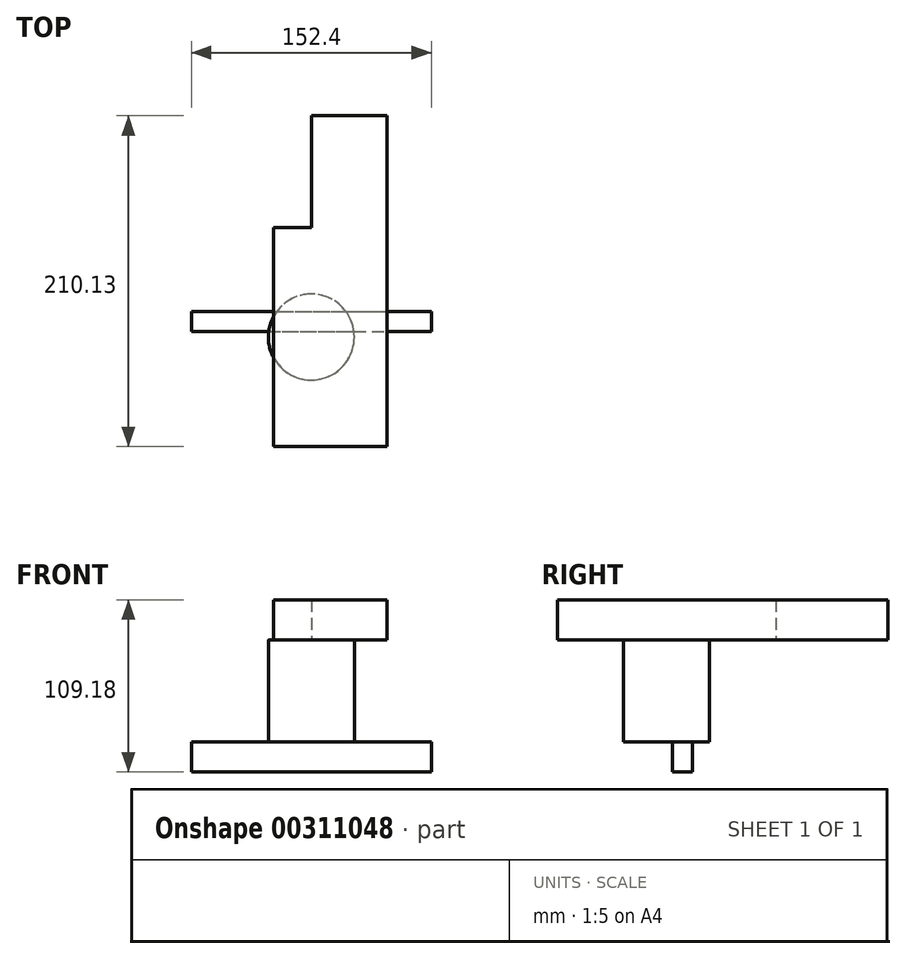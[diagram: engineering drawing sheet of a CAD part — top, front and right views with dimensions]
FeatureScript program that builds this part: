
annotation { "Feature Type Name" : "Feature", "Feature Type Description" : "" }
export const myFeature = defineFeature(function(context is Context, id is Id, definition is map)
    precondition{}
    {
        {
            var Q0;
            Q0=qCreatedBy(makeId("Front.planeOp"),FACE);
            var sketch = newSketch(context, id + "F0", { "sketchPlane" : qUnion([Q0])});
            skLineSegment(sketch, "E0.bottom", {"start": v(-76.2, -9.53) * mm, "end": v(76.2, -9.53) * mm});
            skLineSegment(sketch, "E0.top", {"start": v(-76.2, 9.53) * mm, "end": v(76.2, 9.53) * mm, "construction": true});
            skLineSegment(sketch, "E0.left", {"start": v(-76.2, 9.53) * mm, "end": v(-76.2, -9.53) * mm});
            skLineSegment(sketch, "E0.right", {"start": v(76.2, 9.53) * mm, "end": v(76.2, -9.52) * mm});
            skPoint(sketch, "E0.middle", {"position": v(0, 0) * mm});
            skLineSegment(sketch, "E1", {"start": v(-76.2, 9.53) * mm, "end": v(76.2, 9.53) * mm});
            skSolve(sketch);
        }
        {
            var Q0;
            Q0 = qSketchRegion(id + "F0", true);
            extrude(context, id + "F1", {"entities" : qUnion([Q0]), "depth" : 12.7 * mm});
        }
        {
            var Q0;
            Q0=makeQuery(id+"F1.opExtrude","SWEPT_FACE",FACE,{"disambiguationData":[OSD([sQuery(id+"F0.wireOp",EDGE,"E1")])]});
            var sketch = newSketch(context, id + "F2", { "sketchPlane" : qUnion([Q0])});
            skCircle(sketch, "E2", {"center": v(0, -16.31) * mm, "radius": 27.3 * mm});
            skSolve(sketch);
        }
        {
            var Q0;
            Q0 = qSketchRegion(id + "F2", true);
            extrude(context, id + "F3", {"entities" : qUnion([Q0]), "operationType" : NewBodyOperationType.ADD, "depth" : 64.73 * mm});
        }
        {
            var Q0;
            Q0=makeQuery(id+"F3.opExtrude","CAP_FACE",FACE,{"disambiguationData":[OSD([sQuery(id+"F2.wireOp",EDGE,"E2")])],"isStart":false});
            var sketch = newSketch(context, id + "F4", { "sketchPlane" : qUnion([Q0])});
            skLineSegment(sketch, "E3.bottom", {"start": v(0, -16.31) * mm, "end": v(0, -16.31) * mm});
            skLineSegment(sketch, "E3.top", {"start": v(0, -16.31) * mm, "end": v(0, -16.31) * mm});
            skLineSegment(sketch, "E3.left", {"start": v(0, -16.31) * mm, "end": v(0, -16.31) * mm});
            skLineSegment(sketch, "E3.right", {"start": v(0, -16.31) * mm, "end": v(0, -16.31) * mm});
            skPoint(sketch, "E3.middle", {"position": v(0, -16.31) * mm});
            skLineSegment(sketch, "E4.bottom", {"start": v(24.05, -85.81) * mm, "end": v(-24.05, -85.81) * mm});
            skLineSegment(sketch, "E4.top", {"start": v(24.05, 53.2) * mm, "end": v(-24.05, 53.2) * mm});
            skLineSegment(sketch, "E4.left", {"start": v(24.05, -85.81) * mm, "end": v(24.05, 53.2) * mm});
            skLineSegment(sketch, "E4.right", {"start": v(-24.05, -85.81) * mm, "end": v(-24.05, 53.2) * mm});
            skLineSegment(sketch, "E5.bottom", {"start": v(0, -85.81) * mm, "end": v(48.1, -85.81) * mm});
            skLineSegment(sketch, "E5.top", {"start": v(0, 124.32) * mm, "end": v(48.1, 124.32) * mm});
            skLineSegment(sketch, "E5.left", {"start": v(0, -85.81) * mm, "end": v(0, 124.32) * mm});
            skLineSegment(sketch, "E5.right", {"start": v(48.1, -85.81) * mm, "end": v(48.1, 124.32) * mm});
            skPoint(sketch, "E5.middle", {"position": v(24.05, 19.25) * mm});
            skSolve(sketch);
        }
        {
            var Q0;
            Q0 = qSketchRegion(id + "F4", true);
            extrude(context, id + "F5", {"entities" : qUnion([Q0]), "operationType" : NewBodyOperationType.ADD, "depth" : 25.4 * mm, "offsetDistance" : 25.4 * mm});
        }
    });
